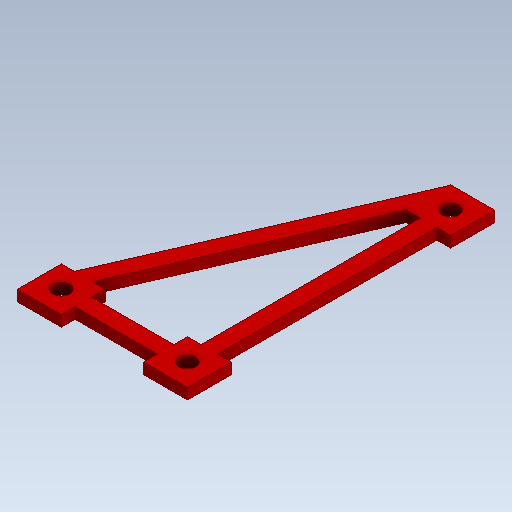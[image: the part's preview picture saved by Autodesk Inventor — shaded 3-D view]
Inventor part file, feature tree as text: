
AUTODESK INVENTOR PART (.ipt)
format: ipt  version: 2020 (Build 240168000, 168)  size: 153,088 bytes
history: native  units: mm
features: sketch x2, other x1, extrude x1
ambient origin geometry x8: Origin, YZ Plane, XZ Plane, XY Plane, X Axis, Y Axis, Z Axis, Center Point
bodies: Solid1 (feature_tree)
feature tree (4):
  other  "HexBodyV2.ipt"
  extrude  "Extrusion1"  Depth=10.0mm
  sketch  "Sketch14"  dims[d2=3.1mm d3=3.1mm d4=3.0mm d5=3.0mm d6=3.0mm d7=2.0mm d8=0.0mm]
  sketch  "Sketch2"  dims[d0=10.0mm d1=3.1mm]
